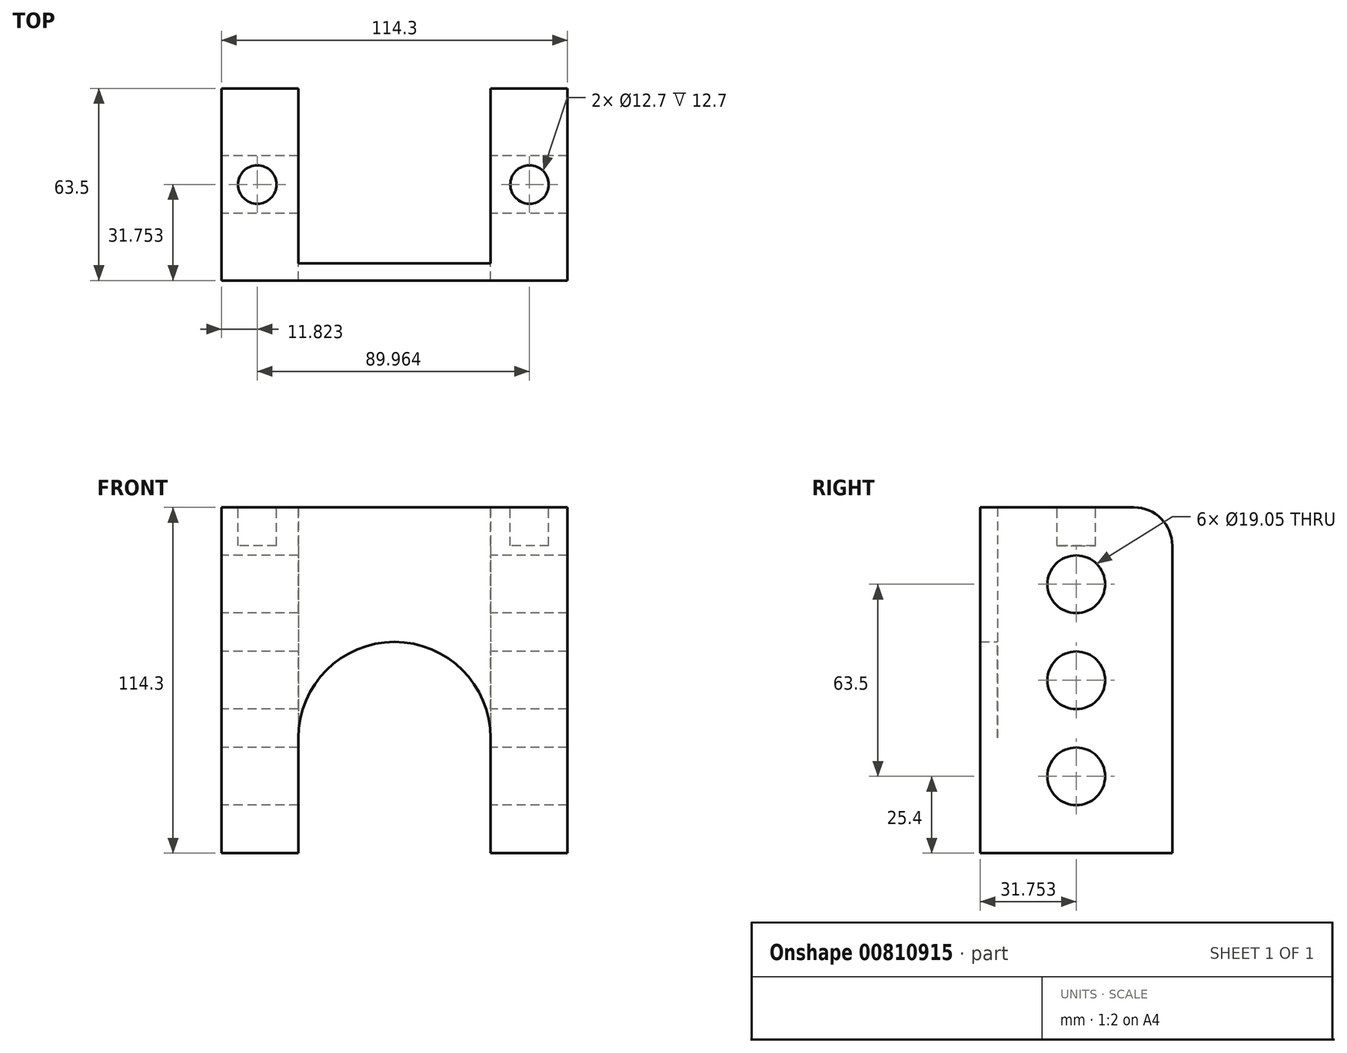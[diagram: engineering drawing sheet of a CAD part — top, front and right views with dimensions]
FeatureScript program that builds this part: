
annotation { "Feature Type Name" : "Feature", "Feature Type Description" : "" }
export const myFeature = defineFeature(function(context is Context, id is Id, definition is map)
    precondition{}
    {
        {
            var Q0;
            Q0=qCreatedBy(makeId("Top.planeOp"),FACE);
            var sketch = newSketch(context, id + "F0", { "sketchPlane" : qUnion([Q0])});
            skLineSegment(sketch, "E0.bottom", {"start": v(-57.15, 57.82) * mm, "end": v(-31.75, 57.82) * mm});
            skLineSegment(sketch, "E0.top", {"start": v(-57.15, -5.68) * mm, "end": v(57.15, -5.68) * mm});
            skLineSegment(sketch, "E0.left", {"start": v(-57.15, 57.82) * mm, "end": v(-57.15, -5.68) * mm});
            skLineSegment(sketch, "E0.right", {"start": v(57.15, 57.82) * mm, "end": v(57.15, -5.68) * mm});
            skLineSegment(sketch, "E1.top", {"start": v(-31.75, 0) * mm, "end": v(31.75, 0) * mm});
            skLineSegment(sketch, "E1.left", {"start": v(-31.75, 57.82) * mm, "end": v(-31.75, 0) * mm});
            skLineSegment(sketch, "E1.right", {"start": v(31.75, 57.82) * mm, "end": v(31.75, 0) * mm});
            skLineSegment(sketch, "E2.trimOffspring", {"start": v(31.75, 57.82) * mm, "end": v(57.15, 57.82) * mm});
            skSolve(sketch);
        }
        {
            var Q0;
            Q0 = qSketchRegion(id + "F0", true);
            extrude(context, id + "F1", {"entities" : qUnion([Q0]), "depth" : 114.3 * mm, "offsetDistance" : 25.4 * mm});
        }
        {
            var Q0;
            Q0=makeQuery(id+"F1.opExtrude","SWEPT_FACE",FACE,{"disambiguationData":[OSD([sQuery(id+"F0.wireOp",EDGE,"E0.left")])]});
            var sketch = newSketch(context, id + "F2", { "sketchPlane" : qUnion([Q0])});
            skCircle(sketch, "E3", {"center": v(-26.07, 25.4) * mm, "radius": 9.53 * mm});
            skCircle(sketch, "E4", {"center": v(-26.07, 88.9) * mm, "radius": 9.53 * mm});
            skCircle(sketch, "E5", {"center": v(-26.07, 57.15) * mm, "radius": 9.53 * mm});
            skSolve(sketch);
        }
        {
            var Q0;
            Q0 = qSketchRegion(id + "F2", true);
            extrude(context, id + "F3", {"entities" : qUnion([Q0]), "operationType" : NewBodyOperationType.REMOVE, "endBound" : BoundingType.THROUGH_ALL, "oppositeDirection" : true, "depth" : 25.4 * mm, "offsetDistance" : 25.4 * mm});
        }
        {
            var Q0;
            Q0=makeQuery(id+"F1.opExtrude","SWEPT_FACE",FACE,{"disambiguationData":[OSD([sQuery(id+"F0.wireOp",EDGE,"E1.top")])]});
            var sketch = newSketch(context, id + "F4", { "sketchPlane" : qUnion([Q0])});
            skLineSegment(sketch, "E6.bottom", {"start": v(-31.75, 0) * mm, "end": v(31.75, 0) * mm});
            skLineSegment(sketch, "E6.left", {"start": v(-31.75, 0) * mm, "end": v(-31.75, 38.1) * mm});
            skLineSegment(sketch, "E6.right", {"start": v(31.75, 0) * mm, "end": v(31.75, 38.1) * mm});
            skArc(sketch, "E7", {"start": v(31.75, 38.1) * mm, "mid": v(0, 69.85) * mm, "end": v(-31.75, 38.1) * mm});
            skSolve(sketch);
        }
        {
            var Q0;
            Q0 = qSketchRegion(id + "F4", true);
            extrude(context, id + "F5", {"entities" : qUnion([Q0]), "operationType" : NewBodyOperationType.REMOVE, "endBound" : BoundingType.THROUGH_ALL, "oppositeDirection" : true, "depth" : 25.4 * mm, "offsetDistance" : 25.4 * mm});
        }
        {
            var Q0;
            Q0=makeQuery(id+"F1.opExtrude","CAP_EDGE",EDGE,{"disambiguationData":[OSD([sQuery(id+"F0.wireOp",EDGE,"E2.trimOffspring")])],"isStart":false});
            var Q1;
            Q1=makeQuery(id+"F1.opExtrude","CAP_EDGE",EDGE,{"disambiguationData":[OSD([sQuery(id+"F0.wireOp",EDGE,"E0.bottom")])],"isStart":false});
            fillet(context, id + "F6", {"entities" : qUnion([Q0, Q1]), "radius" : 12.7 * mm, "tangentPropagation" : true, "allowEdgeOverflow" : false});
        }
        {
            var Q0;
            Q0=makeQuery(id+"F1.opExtrude","CAP_FACE",FACE,{"disambiguationData":[OSD([sQuery(id+"F0.wireOp",EDGE,"E0.bottom"),sQuery(id+"F0.wireOp",EDGE,"E0.top"),sQuery(id+"F0.wireOp",EDGE,"E0.left"),sQuery(id+"F0.wireOp",EDGE,"E0.right"),sQuery(id+"F0.wireOp",EDGE,"E1.top"),sQuery(id+"F0.wireOp",EDGE,"E1.left"),sQuery(id+"F0.wireOp",EDGE,"E1.right"),sQuery(id+"F0.wireOp",EDGE,"E2.trimOffspring")])],"isStart":false});
            var sketch = newSketch(context, id + "F7", { "sketchPlane" : qUnion([Q0])});
            skCircle(sketch, "E8", {"center": v(-45.33, 26.07) * mm, "radius": 6.35 * mm});
            skCircle(sketch, "E9", {"center": v(44.64, 26.07) * mm, "radius": 6.35 * mm});
            skSolve(sketch);
        }
        {
            var Q0;
            Q0 = qSketchRegion(id + "F7", true);
            extrude(context, id + "F8", {"entities" : qUnion([Q0]), "operationType" : NewBodyOperationType.REMOVE, "oppositeDirection" : true, "depth" : 12.7 * mm, "offsetDistance" : 25.4 * mm});
        }
    });
